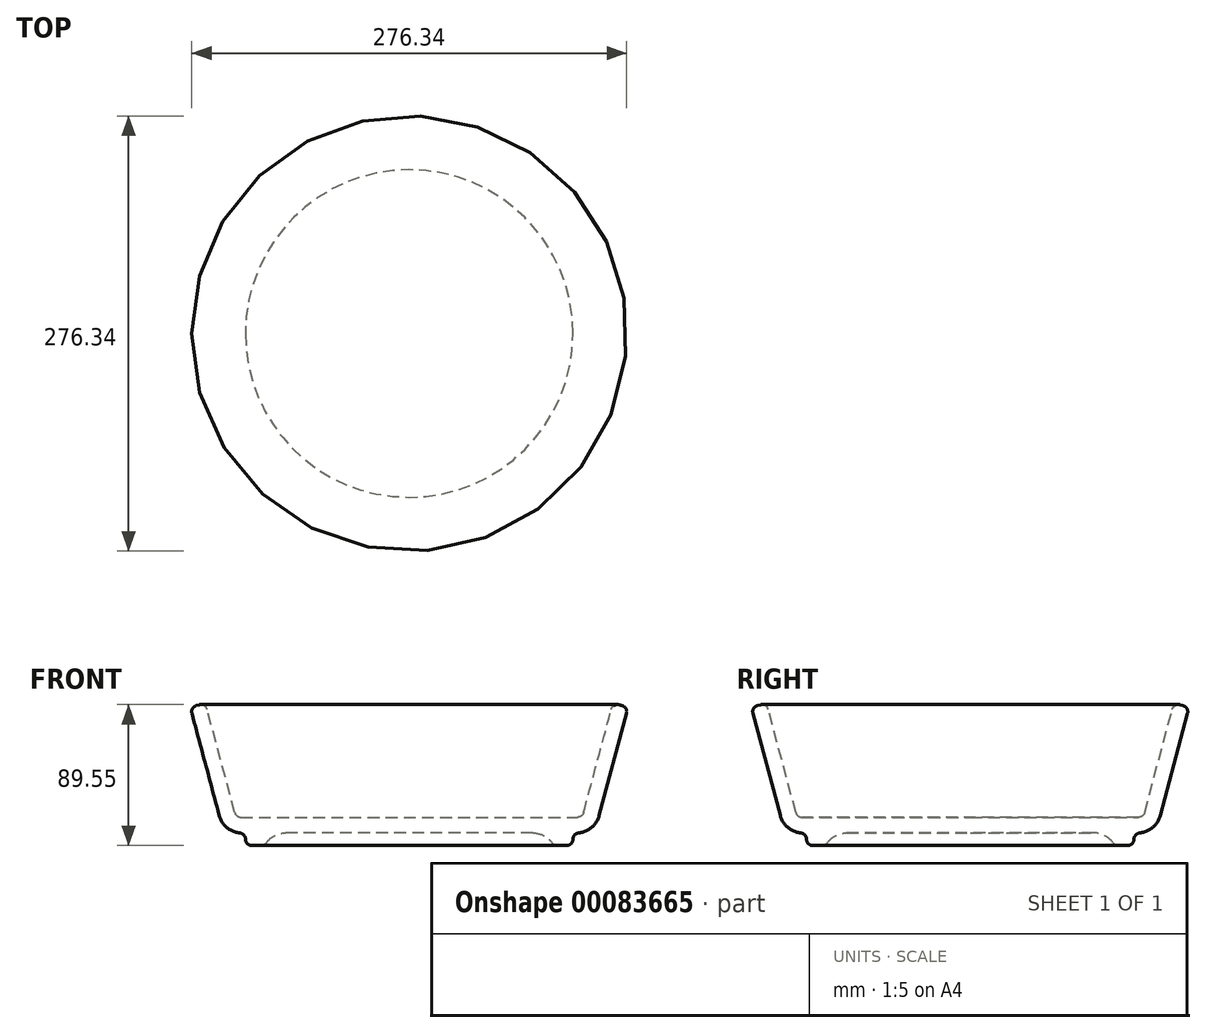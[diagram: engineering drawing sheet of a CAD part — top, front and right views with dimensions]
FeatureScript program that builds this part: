
annotation { "Feature Type Name" : "Feature", "Feature Type Description" : "" }
export const myFeature = defineFeature(function(context is Context, id is Id, definition is map)
    precondition{}
    {
        {
            var Q0;
            Q0=qCreatedBy(makeId("Front.planeOp"),FACE);
            var sketch = newSketch(context, id + "F0", { "sketchPlane" : qUnion([Q0])});
            skLineSegment(sketch, "E0", {"start": v(0, 0) * mm, "end": v(-90, 0) * mm});
            skLineSegment(sketch, "E1", {"start": v(-90, 0) * mm, "end": v(-90, -8) * mm});
            skLineSegment(sketch, "E2", {"start": v(-90, -8) * mm, "end": v(-104, -8) * mm});
            skLineSegment(sketch, "E3", {"start": v(-117.67, 0) * mm, "end": v(-139.07, 79.86) * mm});
            skLineSegment(sketch, "E4", {"start": v(-139.07, 79.86) * mm, "end": v(-129.41, 82.44) * mm});
            skLineSegment(sketch, "E5", {"start": v(-129.41, 82.44) * mm, "end": v(-110, 10) * mm});
            skLineSegment(sketch, "E6", {"start": v(-110, 10) * mm, "end": v(0, 10) * mm});
            skLineSegment(sketch, "E7", {"start": v(0, 10) * mm, "end": v(0, 0) * mm});
            skLineSegment(sketch, "E8", {"start": v(-117.67, 0) * mm, "end": v(-104, 0) * mm});
            skLineSegment(sketch, "E9", {"start": v(-104, 0) * mm, "end": v(-104, -8) * mm});
            skSolve(sketch);
        }
        {
            var Q0;
            Q0=makeQuery(id+"F0.imprint","IMPRINT",FACE,{"disambiguationData":[TD([[makeQuery(id+"F0.imprint","IMPRINT",EDGE,{"derivedFrom":sQuery(id+"F0.wireOp",EDGE,"E0")}),-1.0]])]});
            var Q1;
            Q1=sQuery(id+"F0.wireOp",EDGE,"E7");
            revolve(context, id + "F1", {"entities" : qUnion([Q0]), "axis" : qUnion([Q1]), "revolveType" : RevolveType.FULL});
        }
        {
            var Q0;
            Q0=makeQuery(id+"F1.opRevolve","SWEPT_EDGE",EDGE,{"disambiguationData":[OSD([sQuery(id+"F0.wireOp",EDGE,"E5"),sQuery(id+"F0.wireOp",EDGE,"E6")])]});
            var Q1;
            Q1=makeQuery(id+"F1.opRevolve","SWEPT_EDGE",EDGE,{"disambiguationData":[OSD([sQuery(id+"F0.wireOp",EDGE,"E4"),sQuery(id+"F0.wireOp",EDGE,"E5")])]});
            var Q2;
            Q2=makeQuery(id+"F1.opRevolve","SWEPT_EDGE",EDGE,{"disambiguationData":[OSD([sQuery(id+"F0.wireOp",EDGE,"E3"),sQuery(id+"F0.wireOp",EDGE,"E4")])]});
            var Q3;
            Q3=makeQuery(id+"F1.opRevolve","SWEPT_EDGE",EDGE,{"disambiguationData":[OSD([sQuery(id+"F0.wireOp",EDGE,"E2"),sQuery(id+"F0.wireOp",EDGE,"E9")])]});
            var Q4;
            Q4=makeQuery(id+"F1.opRevolve","SWEPT_EDGE",EDGE,{"disambiguationData":[OSD([sQuery(id+"F0.wireOp",EDGE,"E1"),sQuery(id+"F0.wireOp",EDGE,"E2")])]});
            var Q5;
            Q5=makeQuery(id+"F1.opRevolve","SWEPT_EDGE",EDGE,{"disambiguationData":[OSD([sQuery(id+"F0.wireOp",EDGE,"E8"),sQuery(id+"F0.wireOp",EDGE,"E9")])]});
            fillet(context, id + "F2", {"entities" : qUnion([Q0, Q1, Q2, Q3, Q4, Q5]), "radius" : 4 * mm, "tangentPropagation" : true, "allowEdgeOverflow" : false});
        }
        {
            var Q0;
            Q0=makeQuery(id+"F1.opRevolve","SWEPT_FACE",FACE,{"disambiguationData":[OSD([sQuery(id+"F0.wireOp",EDGE,"E0")])]});
            var Q1;
            Q1=makeQuery(id+"F1.opRevolve","SWEPT_EDGE",EDGE,{"disambiguationData":[OSD([sQuery(id+"F0.wireOp",EDGE,"E3"),sQuery(id+"F0.wireOp",EDGE,"E8")])]});
            fillet(context, id + "F3", {"entities" : qUnion([Q0, Q1]), "radius" : 15 * mm, "tangentPropagation" : true, "allowEdgeOverflow" : false});
        }
    });
